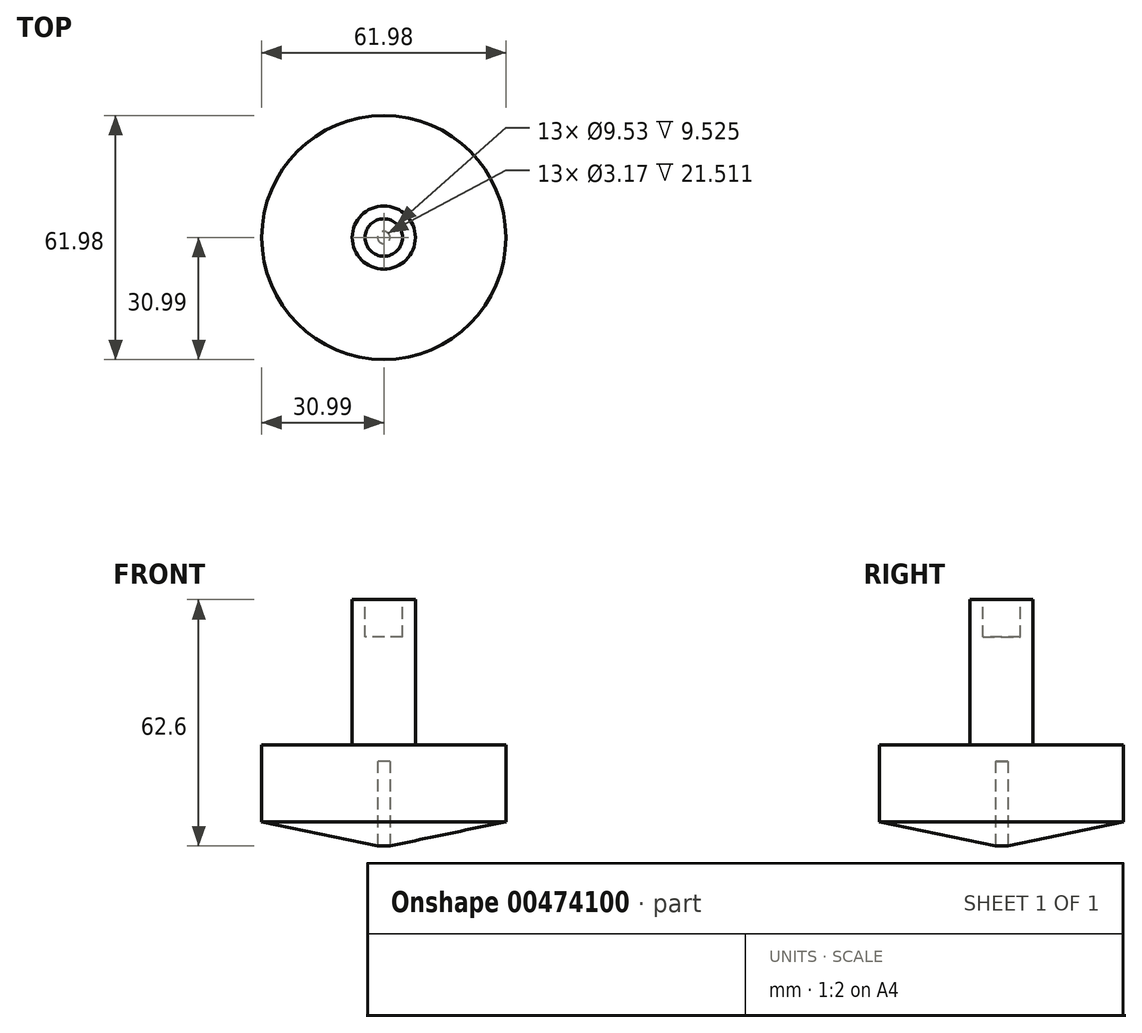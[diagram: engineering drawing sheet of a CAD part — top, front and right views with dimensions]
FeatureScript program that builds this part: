
annotation { "Feature Type Name" : "Feature", "Feature Type Description" : "" }
export const myFeature = defineFeature(function(context is Context, id is Id, definition is map)
    precondition{}
    {
        {
            var Q0;
            Q0=qCreatedBy(makeId("Front.planeOp"),FACE);
            var sketch = newSketch(context, id + "F0", { "sketchPlane" : qUnion([Q0])});
            skLineSegment(sketch, "E0", {"start": v(0, 0) * mm, "end": v(31, 6.5) * mm});
            skLineSegment(sketch, "E1", {"start": v(31, 6.5) * mm, "end": v(31, 25.98) * mm});
            skLineSegment(sketch, "E2", {"start": v(31, 25.98) * mm, "end": v(8.01, 25.98) * mm});
            skLineSegment(sketch, "E3", {"start": v(8.01, 25.98) * mm, "end": v(8.01, 62.93) * mm});
            skLineSegment(sketch, "E4", {"start": v(8.01, 62.93) * mm, "end": v(0, 62.93) * mm});
            skLineSegment(sketch, "E5", {"start": v(0, 62.93) * mm, "end": v(0, 0) * mm});
            skSolve(sketch);
        }
        {
            var Q0;
            Q0=makeQuery(id+"F0.imprint","IMPRINT",FACE,{"disambiguationData":[TD([[makeQuery(id+"F0.imprint","IMPRINT",EDGE,{"derivedFrom":sQuery(id+"F0.wireOp",EDGE,"E0")}),1.0]])]});
            var Q1;
            Q1=sQuery(id+"F0.wireOp",EDGE,"E5");
            revolve(context, id + "F1", {"entities" : qUnion([Q0]), "axis" : qUnion([Q1]), "revolveType" : RevolveType.FULL});
        }
        {
            var Q0;
            Q0=makeQuery(id+"F1.opRevolve","SWEPT_FACE",FACE,{"disambiguationData":[OSD([sQuery(id+"F0.wireOp",EDGE,"E4")])]});
            var sketch = newSketch(context, id + "F2", { "sketchPlane" : qUnion([Q0])});
            skCircle(sketch, "E6", {"center": v(0, 0) * mm, "radius": 4.76 * mm});
            skSolve(sketch);
        }
        {
            var Q0;
            Q0=makeQuery(id+"F2.imprint","IMPRINT",FACE,{"disambiguationData":[TD([[makeQuery(id+"F2.imprint","IMPRINT",EDGE,{"derivedFrom":sQuery(id+"F2.wireOp",EDGE,"E6")}),1.0]])]});
            extrude(context, id + "F3", {"entities" : qUnion([Q0]), "operationType" : NewBodyOperationType.REMOVE, "oppositeDirection" : true, "depth" : 9.52 * mm});
        }
        {
            var Q0;
            Q0=qCreatedBy(makeId("Top.planeOp"),FACE);
            var sketch = newSketch(context, id + "F4", { "sketchPlane" : qUnion([Q0])});
            skCircle(sketch, "E7", {"center": v(0, 0) * mm, "radius": 1.59 * mm});
            skSolve(sketch);
        }
        {
            var Q0;
            Q0=makeQuery(id+"F4.imprint","IMPRINT",FACE,{"disambiguationData":[TD([[makeQuery(id+"F4.imprint","IMPRINT",EDGE,{"derivedFrom":sQuery(id+"F4.wireOp",EDGE,"E7")}),1.0]])]});
            extrude(context, id + "F5", {"entities" : qUnion([Q0]), "operationType" : NewBodyOperationType.REMOVE, "oppositeDirection" : true, "depth" : -21.84 * mm});
        }
    });
